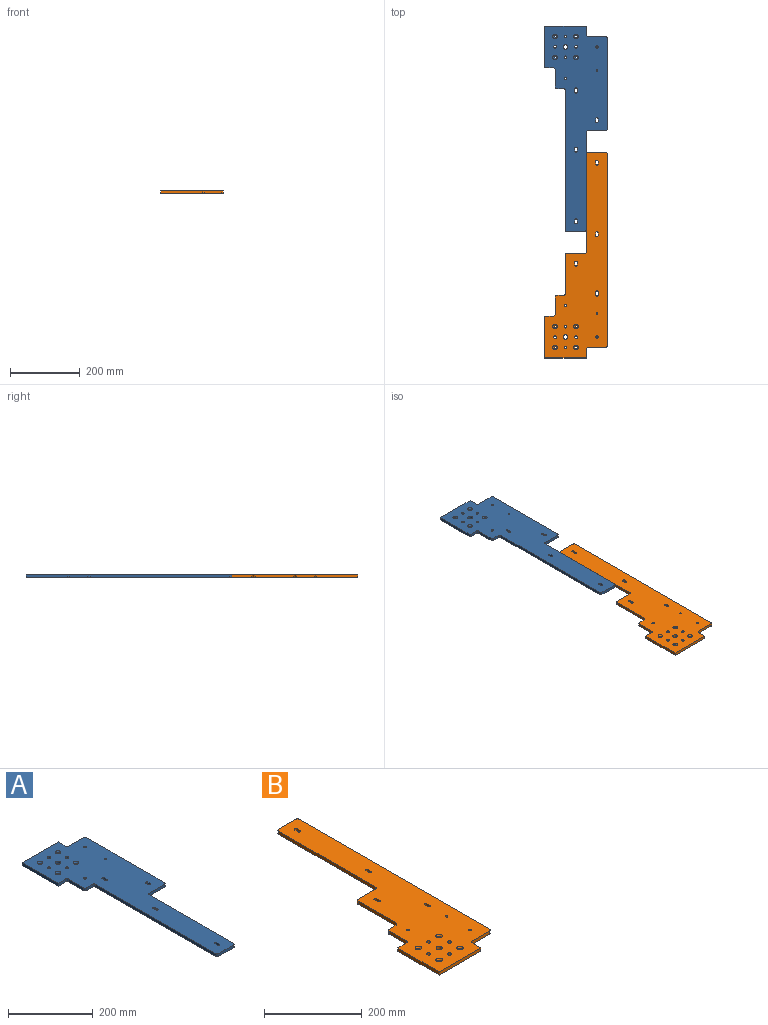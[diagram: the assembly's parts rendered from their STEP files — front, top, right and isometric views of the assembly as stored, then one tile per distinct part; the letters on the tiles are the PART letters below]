
ASSEMBLY  parts=2 mates=2
PART A: 73 faces, bbox 180x590x8 mm
  f0: plane 590x180mm, normal (0,0,1), area 59101.7mm2, adj f1,f2,f3,f4,f5,f6,f7,f8
  f1: plane 120x8mm, normal (0,1,0), area 960mm2, adj f0,f2,f12,f14
  f2: plane 25x8mm, normal (1,0,0), area 200mm2, adj f0,f1,f3,f12
  f3: cylinder r=5mm len=8mm, axis (0,0,-1), area 62.8mm2, adj f0,f2,f4,f12
  f4: plane 50x8mm, normal (0,1,0), area 400mm2, adj f0,f3,f5,f12
  f5: cylinder r=5mm len=8mm, axis (0,0,-1), area 62.8mm2, adj f0,f4,f6,f12
  f6: plane 260x8mm, normal (1,0,0), area 2080mm2, adj f0,f5,f12,f33
  f7: plane 400x8mm, normal (-1,0,0), area 3200mm2, adj f0,f8,f12,f35
  f8: cylinder r=5mm len=8mm, axis (0,0,-1), area 62.8mm2, adj f0,f7,f9,f12
  f9: plane 20x8mm, normal (0,-1,0), area 160mm2, adj f0,f8,f10,f12
  f10: cylinder r=5mm len=8mm, axis (0,0,-1), area 62.8mm2, adj f0,f9,f11,f12
  f11: plane 50x8mm, normal (-1,0,0), area 400mm2, adj f0,f10,f12,f13
  f12: plane 590x180mm, normal (0,0,-1), area 58656.6mm2, adj f1,f2,f3,f4,f5,f6,f7,f8
  f13: cylinder r=5mm len=8mm, axis (0,0,-1), area 62.8mm2, adj f0,f11,f12,f15
  f14: plane 120x8mm, normal (-1,0,0), area 960mm2, adj f0,f1,f12,f15
  f15: plane 25x8mm, normal (0,-1,0), area 200mm2, adj f0,f12,f13,f14
  f16: cylinder r=6.5mm len=13mm, axis (0,0,-1), area 326.7mm2, adj f0,f12
  f17: cylinder r=4mm len=8mm, axis (0,0,-1), area 201.1mm2, adj f0,f12
  f18: cylinder r=4mm len=8mm, axis (0,0,-1), area 201.1mm2, adj f0,f12
  f19: cylinder r=4mm len=8mm, axis (0,0,-1), area 201.1mm2, adj f0,f12
  f20: cylinder r=4mm len=8mm, axis (0,0,-1), area 201.1mm2, adj f0,f12
  f21: cylinder r=3.3mm len=6.6mm, axis (0,0,1), area 95mm2, adj f12,f22
  f22: cone r=3.3mm half-angle=45deg, axis (0,0,1), area 152.3mm2, adj f0,f21
  f23: cylinder r=3.3mm len=6.6mm, axis (0,0,1), area 95mm2, adj f12,f24
  f24: cone r=3.3mm half-angle=45deg, axis (0,0,1), area 152.3mm2, adj f0,f23
  f25: cylinder r=3.3mm len=6.6mm, axis (0,0,1), area 95mm2, adj f12,f26
  f26: cone r=3.3mm half-angle=45deg, axis (0,0,1), area 152.3mm2, adj f0,f25
  f27: cylinder r=3.3mm len=6.6mm, axis (0,0,1), area 95mm2, adj f12,f28
  f28: cone r=3.3mm half-angle=45deg, axis (0,0,1), area 152.3mm2, adj f0,f27
  f29: cylinder r=5mm len=8mm, axis (0,0,-1), area 62.8mm2, adj f0,f12,f30,f34
  f30: plane 280x8mm, normal (1,0,0), area 2240mm2, adj f0,f12,f29,f31
  f31: cylinder r=5mm len=8mm, axis (0,0,-1), area 62.8mm2, adj f0,f12,f30,f32
  f32: plane 50.5x8mm, normal (0,-1,0), area 404mm2, adj f0,f12,f31,f33
  f33: cylinder r=5mm len=8mm, axis (0,0,-1), area 62.8mm2, adj f0,f6,f12,f32
  f34: plane 49.5x8mm, normal (0,-1,0), area 396mm2, adj f0,f12,f29,f35
  f35: cylinder r=5mm len=8mm, axis (0,0,-1), area 62.8mm2, adj f0,f7,f12,f34
  f36: cylinder r=2.5mm len=8mm, axis (0,0,-1), area 125.7mm2, adj f0,f12
  f37: cylinder r=3.3mm len=6.6mm, axis (0,0,-1), area 95mm2, adj f0,f38
  f38: cone r=3.3mm half-angle=45deg, axis (0,0,-1), area 152.3mm2, adj f12,f37
  f39: cylinder r=3.3mm len=6.6mm, axis (0,0,-1), area 95mm2, adj f0,f40
  f40: cone r=3.3mm half-angle=45deg, axis (0,0,-1), area 152.3mm2, adj f12,f39
  f41: cylinder r=3.3mm len=6.6mm, axis (0,0,-1), area 47.5mm2, adj f0,f42,f44,f58
  f42: plane 8.4x4.58mm, normal (-1,0,0), area 38.5mm2, adj f0,f41,f43,f57
  f43: cylinder r=3.3mm len=6.6mm, axis (0,0,-1), area 47.5mm2, adj f0,f42,f44,f59
  f44: plane 8.4x4.58mm, normal (1,0,0), area 38.5mm2, adj f0,f41,f43,f60
  f45: cylinder r=3.3mm len=6.6mm, axis (0,0,-1), area 47.5mm2, adj f0,f46,f48,f62
  f46: plane 8.4x4.58mm, normal (-1,0,0), area 38.5mm2, adj f0,f45,f47,f61
  f47: cylinder r=3.3mm len=6.6mm, axis (0,0,-1), area 47.5mm2, adj f0,f46,f48,f63
  f48: plane 8.4x4.58mm, normal (1,0,0), area 38.5mm2, adj f0,f45,f47,f64
  f49: cylinder r=3.3mm len=6.6mm, axis (0,0,-1), area 47.5mm2, adj f0,f50,f52,f66
  f50: plane 8.4x4.58mm, normal (-1,0,0), area 38.5mm2, adj f0,f49,f51,f65
  f51: cylinder r=3.3mm len=6.6mm, axis (0,0,-1), area 47.5mm2, adj f0,f50,f52,f67
  f52: plane 8.4x4.58mm, normal (1,0,0), area 38.5mm2, adj f0,f49,f51,f68
  f53: cylinder r=3.3mm len=6.6mm, axis (0,0,-1), area 47.5mm2, adj f0,f54,f56,f70
  f54: plane 8.4x4.58mm, normal (-1,0,0), area 38.5mm2, adj f0,f53,f55,f69
  f55: cylinder r=3.3mm len=6.6mm, axis (0,0,-1), area 47.5mm2, adj f0,f54,f56,f71
  f56: plane 8.4x4.58mm, normal (1,0,0), area 38.5mm2, adj f0,f53,f55,f72
  f57: plane 8.4x3.42mm, normal (-0.71,0,-0.71), area 40.6mm2, adj f12,f42,f58,f59
  f58: cone r=3.3mm half-angle=45deg, axis (0,0,-1), area 76.1mm2, adj f12,f41,f57,f60
  f59: cone r=3.3mm half-angle=45deg, axis (0,0,-1), area 76.1mm2, adj f12,f43,f57,f60
  f60: plane 8.4x3.42mm, normal (0.71,0,-0.71), area 40.6mm2, adj f12,f44,f58,f59
  f61: plane 8.4x3.42mm, normal (-0.71,0,-0.71), area 40.6mm2, adj f12,f46,f62,f63
  f62: cone r=3.3mm half-angle=45deg, axis (0,0,-1), area 76.1mm2, adj f12,f45,f61,f64
  f63: cone r=3.3mm half-angle=45deg, axis (0,0,-1), area 76.1mm2, adj f12,f47,f61,f64
  f64: plane 8.4x3.42mm, normal (0.71,0,-0.71), area 40.6mm2, adj f12,f48,f62,f63
  f65: plane 8.4x3.42mm, normal (-0.71,0,-0.71), area 40.6mm2, adj f12,f50,f66,f67
  f66: cone r=3.3mm half-angle=45deg, axis (0,0,-1), area 76.1mm2, adj f12,f49,f65,f68
  f67: cone r=3.3mm half-angle=45deg, axis (0,0,-1), area 76.1mm2, adj f12,f51,f65,f68
  f68: plane 8.4x3.42mm, normal (0.71,0,-0.71), area 40.6mm2, adj f12,f52,f66,f67
  f69: plane 8.4x3.42mm, normal (-0.71,0,-0.71), area 40.6mm2, adj f12,f54,f70,f71
  f70: cone r=3.3mm half-angle=45deg, axis (0,0,-1), area 76.1mm2, adj f12,f53,f69,f72
  f71: cone r=3.3mm half-angle=45deg, axis (0,0,-1), area 76.1mm2, adj f12,f55,f69,f72
  f72: plane 8.4x3.42mm, normal (0.71,0,-0.71), area 40.6mm2, adj f12,f56,f70,f71
PART B: 73 faces, bbox 180x590x8 mm
  f0: plane 590x180mm, normal (0,0,1), area 59101.7mm2, adj f1,f2,f3,f4,f5,f6,f7,f8
  f1: cylinder r=5mm len=8mm, axis (0,0,-1), area 62.8mm2, adj f0,f2,f7,f10
  f2: plane 280x8mm, normal (-1,0,0), area 2240mm2, adj f0,f1,f3,f10
  f3: cylinder r=5mm len=8mm, axis (0,0,-1), area 62.8mm2, adj f0,f2,f4,f10
  f4: plane 50.5x8mm, normal (0,1,0), area 404mm2, adj f0,f3,f5,f10
  f5: cylinder r=5mm len=8mm, axis (0,0,-1), area 62.8mm2, adj f0,f4,f6,f10
  f6: plane 110x8mm, normal (-1,0,0), area 880mm2, adj f0,f5,f10,f16
  f7: plane 49.5x8mm, normal (0,1,0), area 396mm2, adj f0,f1,f9,f10
  f8: plane 550x8mm, normal (1,0,0), area 4400mm2, adj f0,f9,f10,f15
  f9: cylinder r=5mm len=8mm, axis (0,0,-1), area 62.8mm2, adj f0,f7,f8,f10
  f10: plane 590x180mm, normal (0,0,-1), area 58656.6mm2, adj f1,f2,f3,f4,f5,f6,f7,f8
  f11: plane 120x8mm, normal (0,-1,0), area 960mm2, adj f0,f10,f12,f21
  f12: plane 25x8mm, normal (1,0,0), area 200mm2, adj f0,f10,f11,f13
  f13: cylinder r=5mm len=8mm, axis (0,0,-1), area 62.8mm2, adj f0,f10,f12,f14
  f14: plane 50x8mm, normal (0,-1,0), area 400mm2, adj f0,f10,f13,f15
  f15: cylinder r=5mm len=8mm, axis (0,0,-1), area 62.8mm2, adj f0,f8,f10,f14
  f16: cylinder r=5mm len=8mm, axis (0,0,-1), area 62.8mm2, adj f0,f6,f10,f17
  f17: plane 20x8mm, normal (0,1,0), area 160mm2, adj f0,f10,f16,f18
  f18: cylinder r=5mm len=8mm, axis (0,0,-1), area 62.8mm2, adj f0,f10,f17,f19
  f19: plane 50x8mm, normal (-1,0,0), area 400mm2, adj f0,f10,f18,f20
  f20: cylinder r=5mm len=8mm, axis (0,0,-1), area 62.8mm2, adj f0,f10,f19,f22
  f21: plane 120x8mm, normal (-1,0,0), area 960mm2, adj f0,f10,f11,f22
  f22: plane 25x8mm, normal (0,1,0), area 200mm2, adj f0,f10,f20,f21
  f23: cylinder r=6.5mm len=13mm, axis (0,0,-1), area 326.7mm2, adj f0,f10
  f24: cylinder r=4mm len=8mm, axis (0,0,-1), area 201.1mm2, adj f0,f10
  f25: cylinder r=4mm len=8mm, axis (0,0,-1), area 201.1mm2, adj f0,f10
  f26: cylinder r=4mm len=8mm, axis (0,0,-1), area 201.1mm2, adj f0,f10
  f27: cylinder r=4mm len=8mm, axis (0,0,-1), area 201.1mm2, adj f0,f10
  f28: cylinder r=3.3mm len=6.6mm, axis (0,0,1), area 95mm2, adj f10,f29
  f29: cone r=3.3mm half-angle=45deg, axis (0,0,1), area 152.3mm2, adj f0,f28
  f30: cylinder r=3.3mm len=6.6mm, axis (0,0,1), area 95mm2, adj f10,f31
  f31: cone r=3.3mm half-angle=45deg, axis (0,0,1), area 152.3mm2, adj f0,f30
  f32: cylinder r=3.3mm len=6.6mm, axis (0,0,1), area 95mm2, adj f10,f33
  f33: cone r=3.3mm half-angle=45deg, axis (0,0,1), area 152.3mm2, adj f0,f32
  f34: cylinder r=3.3mm len=6.6mm, axis (0,0,1), area 95mm2, adj f10,f35
  f35: cone r=3.3mm half-angle=45deg, axis (0,0,1), area 152.3mm2, adj f0,f34
  f36: cylinder r=2.5mm len=8mm, axis (0,0,-1), area 125.7mm2, adj f0,f10
  f37: cylinder r=3.3mm len=6.6mm, axis (0,0,-1), area 95mm2, adj f0,f38
  f38: cone r=3.3mm half-angle=45deg, axis (0,0,-1), area 152.3mm2, adj f10,f37
  f39: cylinder r=3.3mm len=6.6mm, axis (0,0,-1), area 95mm2, adj f0,f40
  f40: cone r=3.3mm half-angle=45deg, axis (0,0,-1), area 152.3mm2, adj f10,f39
  f41: cylinder r=3.3mm len=6.6mm, axis (0,0,-1), area 47.5mm2, adj f0,f42,f44,f58
  f42: plane 8.4x4.58mm, normal (-1,0,0), area 38.5mm2, adj f0,f41,f43,f57
  f43: cylinder r=3.3mm len=6.6mm, axis (0,0,-1), area 47.5mm2, adj f0,f42,f44,f59
  f44: plane 8.4x4.58mm, normal (1,0,0), area 38.5mm2, adj f0,f41,f43,f60
  f45: cylinder r=3.3mm len=6.6mm, axis (0,0,-1), area 47.5mm2, adj f0,f46,f48,f62
  f46: plane 8.4x4.58mm, normal (-1,0,0), area 38.5mm2, adj f0,f45,f47,f61
  f47: cylinder r=3.3mm len=6.6mm, axis (0,0,-1), area 47.5mm2, adj f0,f46,f48,f63
  f48: plane 8.4x4.58mm, normal (1,0,0), area 38.5mm2, adj f0,f45,f47,f64
  f49: cylinder r=3.3mm len=6.6mm, axis (0,0,-1), area 47.5mm2, adj f0,f50,f52,f66
  f50: plane 8.4x4.58mm, normal (-1,0,0), area 38.5mm2, adj f0,f49,f51,f65
  f51: cylinder r=3.3mm len=6.6mm, axis (0,0,-1), area 47.5mm2, adj f0,f50,f52,f67
  f52: plane 8.4x4.58mm, normal (1,0,0), area 38.5mm2, adj f0,f49,f51,f68
  f53: cylinder r=3.3mm len=6.6mm, axis (0,0,-1), area 47.5mm2, adj f0,f54,f56,f70
  f54: plane 8.4x4.58mm, normal (-1,0,0), area 38.5mm2, adj f0,f53,f55,f69
  f55: cylinder r=3.3mm len=6.6mm, axis (0,0,-1), area 47.5mm2, adj f0,f54,f56,f71
  f56: plane 8.4x4.58mm, normal (1,0,0), area 38.5mm2, adj f0,f53,f55,f72
  f57: plane 8.4x3.42mm, normal (-0.71,0,-0.71), area 40.6mm2, adj f10,f42,f58,f59
  f58: cone r=3.3mm half-angle=45deg, axis (0,0,-1), area 76.1mm2, adj f10,f41,f57,f60
  f59: cone r=3.3mm half-angle=45deg, axis (0,0,-1), area 76.1mm2, adj f10,f43,f57,f60
  f60: plane 8.4x3.42mm, normal (0.71,0,-0.71), area 40.6mm2, adj f10,f44,f58,f59
  f61: plane 8.4x3.42mm, normal (-0.71,0,-0.71), area 40.6mm2, adj f10,f46,f62,f63
  f62: cone r=3.3mm half-angle=45deg, axis (0,0,-1), area 76.1mm2, adj f10,f45,f61,f64
  f63: cone r=3.3mm half-angle=45deg, axis (0,0,-1), area 76.1mm2, adj f10,f47,f61,f64
  f64: plane 8.4x3.42mm, normal (0.71,0,-0.71), area 40.6mm2, adj f10,f48,f62,f63
  f65: plane 8.4x3.42mm, normal (-0.71,0,-0.71), area 40.6mm2, adj f10,f50,f66,f67
  f66: cone r=3.3mm half-angle=45deg, axis (0,0,-1), area 76.1mm2, adj f10,f49,f65,f68
  f67: cone r=3.3mm half-angle=45deg, axis (0,0,-1), area 76.1mm2, adj f10,f51,f65,f68
  f68: plane 8.4x3.42mm, normal (0.71,0,-0.71), area 40.6mm2, adj f10,f52,f66,f67
  f69: plane 8.4x3.42mm, normal (-0.71,0,-0.71), area 40.6mm2, adj f10,f54,f70,f71
  f70: cone r=3.3mm half-angle=45deg, axis (0,0,-1), area 76.1mm2, adj f10,f53,f69,f72
  f71: cone r=3.3mm half-angle=45deg, axis (0,0,-1), area 76.1mm2, adj f10,f55,f69,f72
  f72: plane 8.4x3.42mm, normal (0.71,0,-0.71), area 40.6mm2, adj f10,f56,f70,f71
PLACE A t=(1350,-107.81,-705)mm
PLACE B t=(1350,-60,-705)mm
MATE planar A.f7 <-> B.f6  axis (-1,0,0) through (-90,7.19,4)mm
MATE planar A.f12 <-> B.f10  axis (0,0,-1) through (-60,207.19,0)mm
